# Revit family: Shower-Column-KOHLER-HydroRail_S-K-76471
name_source: partatom
category: Plumbing Fixtures
revit_build: Autodesk Revit 2015 (Build: 20140606_1530(x64)
units: mm (PartAtom-declared; Revit-internal decimal feet)

## types (2) — shared parameters
ADA Compliant = Yes
Assembly Code = D2010700
CW Connection = Yes
Cold Water Inlet = Cold Water Inlet
Date Modified = 11/21/2017
Default Elevation = 36"
Description = Shower column kit with Awaken, 2.0 gpm
Flow Rate = 2 GPM
HW Connection = No
Height = 6 1/4"
Hot Water Inlet = Hot Water Inlet
Length = 18"
Manufacturer = KOHLER Co.
MasterFormat 1995 = 15410
MasterFormat 2004 = 22.41.23
Material = Premium metal construction
Pressure = 45.00 psi
Product Documentation Link = http://www.us.kohler.com
Product Name = HydroRail-S
Product Page URL = http://www.us.kohler.com
URL = https://www.us.kohler.com
Vent Connection = No
Waste Connection = No
Waste Water Outlet = Waste Water Outlet
Width = 3 7/16"

## per-type parameters (varying)
| type | Finish | Model | Type |
| CP-Polished Chrome | Kohler-Metal-CP-Polished_Chrome | K-76471-CP | 1 |
| BN-Vibrant Brushed Nickel | Kohler-Metal-BN-Vibrant_Brushed_Nickel | K-76471-BN | 2 |

## geometry (parser evidence)
native form markers: Blend x4, Sweep x4
no freeform markers — native parametric forms only
